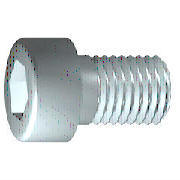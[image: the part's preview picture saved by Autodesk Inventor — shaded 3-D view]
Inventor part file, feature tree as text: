
AUTODESK INVENTOR PART (.ipt)
format: ipt  version: 2025.2 (Build 292293000, 293)  size: 190,976 bytes
history: native  units: mm (DEFAULTED — no unit token found)
features: other x1, extrude x1, chamfer x1, plane x1, fillet x1
ambient origin geometry x7: Origin, YZ Plane, XY Plane, X Axis, Y Axis, Z Axis, Center Point
bodies: Solid1 (feature_tree)
feature tree (5):
  other  "Körper"
  extrude  "Loch"  Depth=18.5mm
  chamfer  "Fase1"  Distance=0.306825mm
  plane  "Work Plane1"
  fillet  "Fillet2"  Radius=3.0mm
